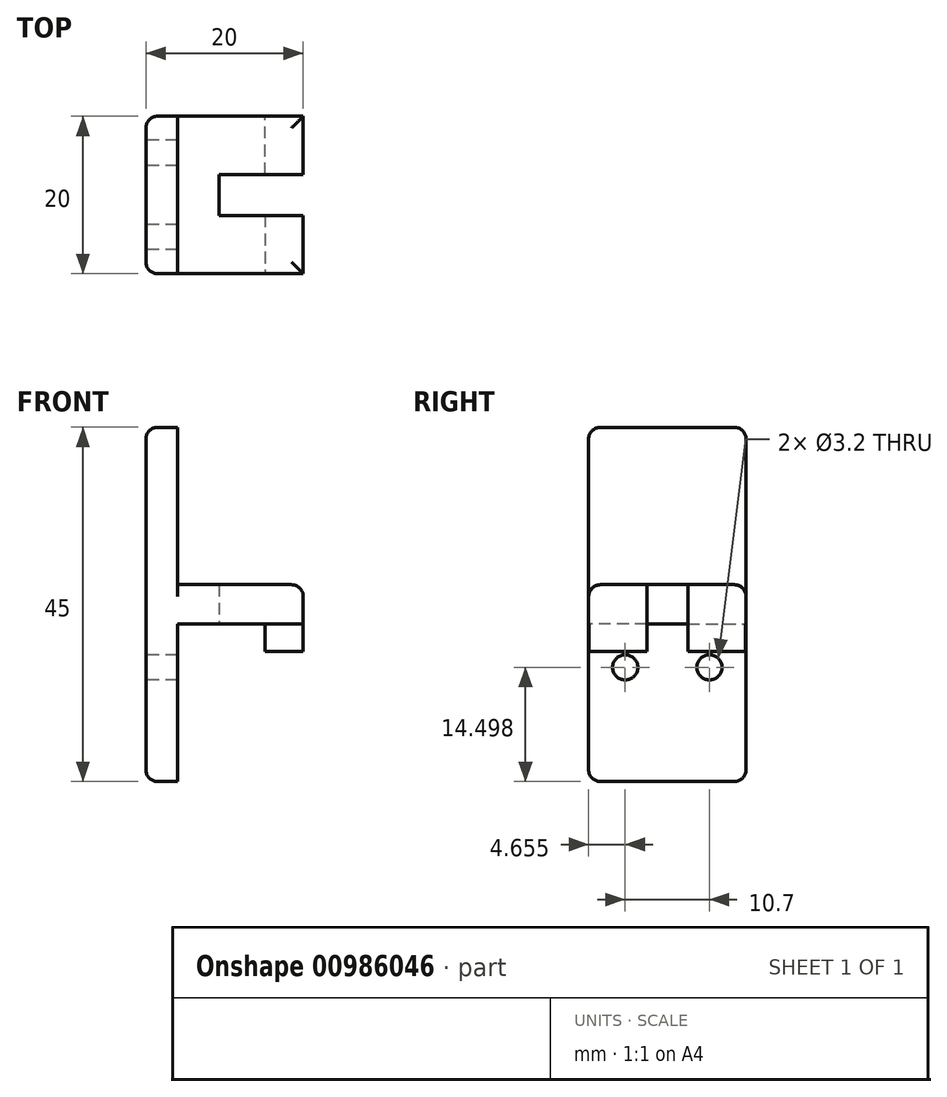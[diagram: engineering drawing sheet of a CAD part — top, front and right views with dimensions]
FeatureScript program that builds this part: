
annotation { "Feature Type Name" : "Feature", "Feature Type Description" : "" }
export const myFeature = defineFeature(function(context is Context, id is Id, definition is map)
    precondition{}
    {
        {
            var Q0;
            Q0=qCreatedBy(makeId("Right.planeOp"),FACE);
            var sketch = newSketch(context, id + "F0", { "sketchPlane" : qUnion([Q0])});
            skLineSegment(sketch, "E0.bottom", {"start": v(3.6, 13.13) * mm, "end": v(-16.4, 13.13) * mm});
            skLineSegment(sketch, "E0.top", {"start": v(3.6, -31.87) * mm, "end": v(-16.4, -31.87) * mm});
            skLineSegment(sketch, "E0.left", {"start": v(3.6, 13.13) * mm, "end": v(3.6, -31.87) * mm});
            skLineSegment(sketch, "E0.right", {"start": v(-16.4, 13.13) * mm, "end": v(-16.4, -31.87) * mm});
            skLineSegment(sketch, "E1.bottom", {"start": v(3.6, -6.87) * mm, "end": v(-16.4, -6.87) * mm});
            skLineSegment(sketch, "E1.top", {"start": v(3.6, -11.87) * mm, "end": v(-16.4, -11.87) * mm});
            skLineSegment(sketch, "E1.left", {"start": v(3.6, -6.87) * mm, "end": v(3.6, -11.87) * mm});
            skLineSegment(sketch, "E1.right", {"start": v(-16.4, -6.87) * mm, "end": v(-16.4, -11.87) * mm});
            skPoint(sketch, "E2", {"position": v(-6.4, 13.13) * mm});
            skLineSegment(sketch, "E3", {"start": v(-6.4, 39.57) * mm, "end": v(-6.4, -58.25) * mm, "construction": true});
            skCircle(sketch, "E4", {"center": v(-1.05, -17.37) * mm, "radius": 1.6 * mm});
            skCircle(sketch, "E5.MirrorC", {"center": v(-11.75, -17.37) * mm, "radius": 1.6 * mm});
            skLineSegment(sketch, "E6.bottom", {"start": v(-16.4, 6.63) * mm, "end": v(-6.4, 6.63) * mm});
            skLineSegment(sketch, "E6.top", {"start": v(-16.4, 2.77) * mm, "end": v(-6.4, 2.77) * mm});
            skLineSegment(sketch, "E6.left", {"start": v(-16.4, 6.63) * mm, "end": v(-16.4, 2.77) * mm});
            skLineSegment(sketch, "E6.right", {"start": v(-6.4, 6.63) * mm, "end": v(-6.4, 2.77) * mm});
            skSolve(sketch);
        }
        {
            var Q0;
            Q0 = qSketchRegion(id + "F0", true);
            extrude(context, id + "F1", {"entities" : qUnion([Q0]), "depth" : 4 * mm, "offsetDistance" : 25 * mm});
        }
        {
            var Q0;
            Q0=makeQuery(id+"F0.imprint","IMPRINT",FACE,{"disambiguationData":[TD([[makeQuery(id+"F0.imprint","IMPRINT",EDGE,{"derivedFrom":sQuery(id+"F0.wireOp",EDGE,"E1.bottom")}),1.0]])]});
            extrude(context, id + "F2", {"entities" : qUnion([Q0]), "operationType" : NewBodyOperationType.ADD, "depth" : 20 * mm, "offsetDistance" : 25 * mm});
        }
        {
            var Q0;
            Q0=makeQuery(id+"F0.imprint","IMPRINT",FACE,{"disambiguationData":[TD([[makeQuery(id+"F0.imprint","IMPRINT",EDGE,{"derivedFrom":sQuery(id+"F0.wireOp",EDGE,"E4")}),1.0]])]});
            extrude(context, id + "F3", {"entities" : qUnion([Q0]), "operationType" : NewBodyOperationType.REMOVE, "endBound" : BoundingType.THROUGH_ALL, "oppositeDirection" : true, "depth" : 25 * mm, "offsetDistance" : 25 * mm});
        }
        {
            var Q0;
            Q0=makeQuery(id+"F1.opExtrude","CAP_EDGE",EDGE,{"disambiguationData":[OSD([sQuery(id+"F0.wireOp",EDGE,"E0.left"),sQuery(id+"F0.wireOp",EDGE,"E1.left")])],"isStart":true});
            var Q1;
            Q1=makeQuery(id+"F1.opExtrude","CAP_EDGE",EDGE,{"disambiguationData":[OSD([sQuery(id+"F0.wireOp",EDGE,"E0.bottom")])],"isStart":true});
            var Q2;
            Q2=makeQuery(id+"F1.opExtrude","CAP_EDGE",EDGE,{"disambiguationData":[OSD([sQuery(id+"F0.wireOp",EDGE,"E0.right"),sQuery(id+"F0.wireOp",EDGE,"E1.right")])],"isStart":true});
            var Q3;
            Q3=makeQuery(id+"F1.opExtrude","CAP_EDGE",EDGE,{"disambiguationData":[OSD([sQuery(id+"F0.wireOp",EDGE,"E0.top")])],"isStart":true});
            var Q4;
            Q4=makeQuery(id+"F1.opExtrude","SWEPT_EDGE",EDGE,{"disambiguationData":[OSD([sQuery(id+"F0.wireOp",EDGE,"E0.bottom"),sQuery(id+"F0.wireOp",EDGE,"E0.left")])]});
            var Q5;
            Q5=makeQuery(id+"F1.opExtrude","SWEPT_EDGE",EDGE,{"disambiguationData":[OSD([sQuery(id+"F0.wireOp",EDGE,"E0.top"),sQuery(id+"F0.wireOp",EDGE,"E0.left")])]});
            var Q6;
            Q6=makeQuery(id+"F1.opExtrude","SWEPT_EDGE",EDGE,{"disambiguationData":[OSD([sQuery(id+"F0.wireOp",EDGE,"E0.bottom"),sQuery(id+"F0.wireOp",EDGE,"E0.right")])]});
            var Q7;
            Q7=makeQuery(id+"F1.opExtrude","SWEPT_EDGE",EDGE,{"disambiguationData":[OSD([sQuery(id+"F0.wireOp",EDGE,"E0.top"),sQuery(id+"F0.wireOp",EDGE,"E0.right")])]});
            var Q8;
            Q8=makeQuery(id+"F2.opExtrude","SWEPT_EDGE",EDGE,{"disambiguationData":[OSD([sQuery(id+"F0.wireOp",EDGE,"E0.right"),sQuery(id+"F0.wireOp",EDGE,"E1.bottom"),sQuery(id+"F0.wireOp",EDGE,"E1.right")])]});
            var Q9;
            Q9=makeQuery(id+"F2.opExtrude","SWEPT_EDGE",EDGE,{"disambiguationData":[OSD([sQuery(id+"F0.wireOp",EDGE,"E0.left"),sQuery(id+"F0.wireOp",EDGE,"E1.bottom"),sQuery(id+"F0.wireOp",EDGE,"E1.left")])]});
            var Q10;
            Q10=makeQuery(id+"F2.opExtrude","CAP_EDGE",EDGE,{"disambiguationData":[OSD([sQuery(id+"F0.wireOp",EDGE,"E1.bottom")])],"isStart":false});
            var Q11;
            Q11=makeQuery(id+"F2.opExtrude","CAP_EDGE",EDGE,{"disambiguationData":[OSD([sQuery(id+"F0.wireOp",EDGE,"E1.left")])],"isStart":false});
            var Q12;
            Q12=makeQuery(id+"F2.opExtrude","CAP_EDGE",EDGE,{"disambiguationData":[OSD([sQuery(id+"F0.wireOp",EDGE,"E1.right")])],"isStart":false});
            fillet(context, id + "F4", {"entities" : qUnion([Q0, Q1, Q2, Q3, Q4, Q5, Q6, Q7, Q8, Q9, Q10, Q11, Q12]), "radius" : 1.5 * mm, "tangentPropagation" : true, "allowEdgeOverflow" : false});
        }
        {
            var Q0;
            Q0=makeQuery(id+"F2.opExtrude","SWEPT_FACE",FACE,{"disambiguationData":[OSD([sQuery(id+"F0.wireOp",EDGE,"E1.top")])]});
            var sketch = newSketch(context, id + "F5", { "sketchPlane" : qUnion([Q0])});
            skPoint(sketch, "E7", {"position": v(20, 6.4) * mm});
            skLineSegment(sketch, "E8", {"start": v(26.97, 6.4) * mm, "end": v(-4.39, 6.4) * mm, "construction": true});
            skLineSegment(sketch, "E9.bottom", {"start": v(20, 9) * mm, "end": v(15.15, 9) * mm});
            skLineSegment(sketch, "E9.top", {"start": v(20, 16.35) * mm, "end": v(15.15, 16.35) * mm});
            skLineSegment(sketch, "E9.left", {"start": v(20, 9) * mm, "end": v(20, 16.35) * mm});
            skLineSegment(sketch, "E9.right", {"start": v(15.15, 9) * mm, "end": v(15.15, 16.35) * mm});
            skLineSegment(sketch, "E10", {"start": v(20, -4.07) * mm, "end": v(20, 19.17) * mm, "construction": true});
            skLineSegment(sketch, "E11.MirrorCS", {"start": v(15.15, 3.8) * mm, "end": v(15.15, -3.56) * mm});
            skLineSegment(sketch, "E12.MirrorCS", {"start": v(20, -3.56) * mm, "end": v(15.15, -3.56) * mm});
            skLineSegment(sketch, "E13.MirrorCS", {"start": v(20, 16.86) * mm, "end": v(20, -6.38) * mm, "construction": true});
            skLineSegment(sketch, "E14.MirrorCS", {"start": v(20, 3.8) * mm, "end": v(15.15, 3.8) * mm});
            skLineSegment(sketch, "E15.bottom", {"start": v(20, 3.8) * mm, "end": v(9.33, 3.8) * mm});
            skLineSegment(sketch, "E15.top", {"start": v(20, 9) * mm, "end": v(9.33, 9) * mm});
            skLineSegment(sketch, "E15.left", {"start": v(20, 3.8) * mm, "end": v(20, 9) * mm});
            skLineSegment(sketch, "E15.right", {"start": v(9.33, 3.8) * mm, "end": v(9.33, 9) * mm});
            skSolve(sketch);
        }
        {
            var Q0;
            {var subQ4=sQuery(id+"F5.wireOp",EDGE,"E9.bottom");Q0=makeQuery(id+"F5.imprint","IMPRINT",FACE,{"disambiguationData":[TD([[makeQuery(id+"F5.imprint","IMPRINT",EDGE,{"derivedFrom":subQ4}),-1.0]])]});}
            var Q1;
            {var subQ6=sQuery(id+"F5.wireOp",EDGE,"E11.MirrorCS");Q1=makeQuery(id+"F5.imprint","IMPRINT",FACE,{"disambiguationData":[TD([[makeQuery(id+"F5.imprint","IMPRINT",EDGE,{"derivedFrom":subQ6}),1.0]])]});}
            extrude(context, id + "F6", {"entities" : qUnion([Q0, Q1]), "operationType" : NewBodyOperationType.ADD, "depth" : 3.5 * mm, "offsetDistance" : 25 * mm});
        }
        {
            var Q0;
            {var subQ3=sQuery(id+"F5.wireOp",EDGE,"E9.right");Q0=makeQuery(id+"F5.imprint","IMPRINT",FACE,{"disambiguationData":[TD([[makeQuery(id+"F5.imprint","IMPRINT",EDGE,{"derivedFrom":subQ3}),-1.0]])]});}
            extrude(context, id + "F7", {"entities" : qUnion([Q0]), "operationType" : NewBodyOperationType.ADD, "depth" : 3.5 * mm, "offsetDistance" : 25 * mm});
        }
        {
            var Q0;
            {var subQ3=sQuery(id+"F5.wireOp",EDGE,"E15.left");Q0=makeQuery(id+"F5.imprint","IMPRINT",FACE,{"disambiguationData":[TD([[makeQuery(id+"F5.imprint","IMPRINT",EDGE,{"derivedFrom":subQ3}),1.0]])]});}
            extrude(context, id + "F8", {"entities" : qUnion([Q0]), "operationType" : NewBodyOperationType.REMOVE, "oppositeDirection" : true, "depth" : 25 * mm, "offsetDistance" : 25 * mm});
        }
    });
